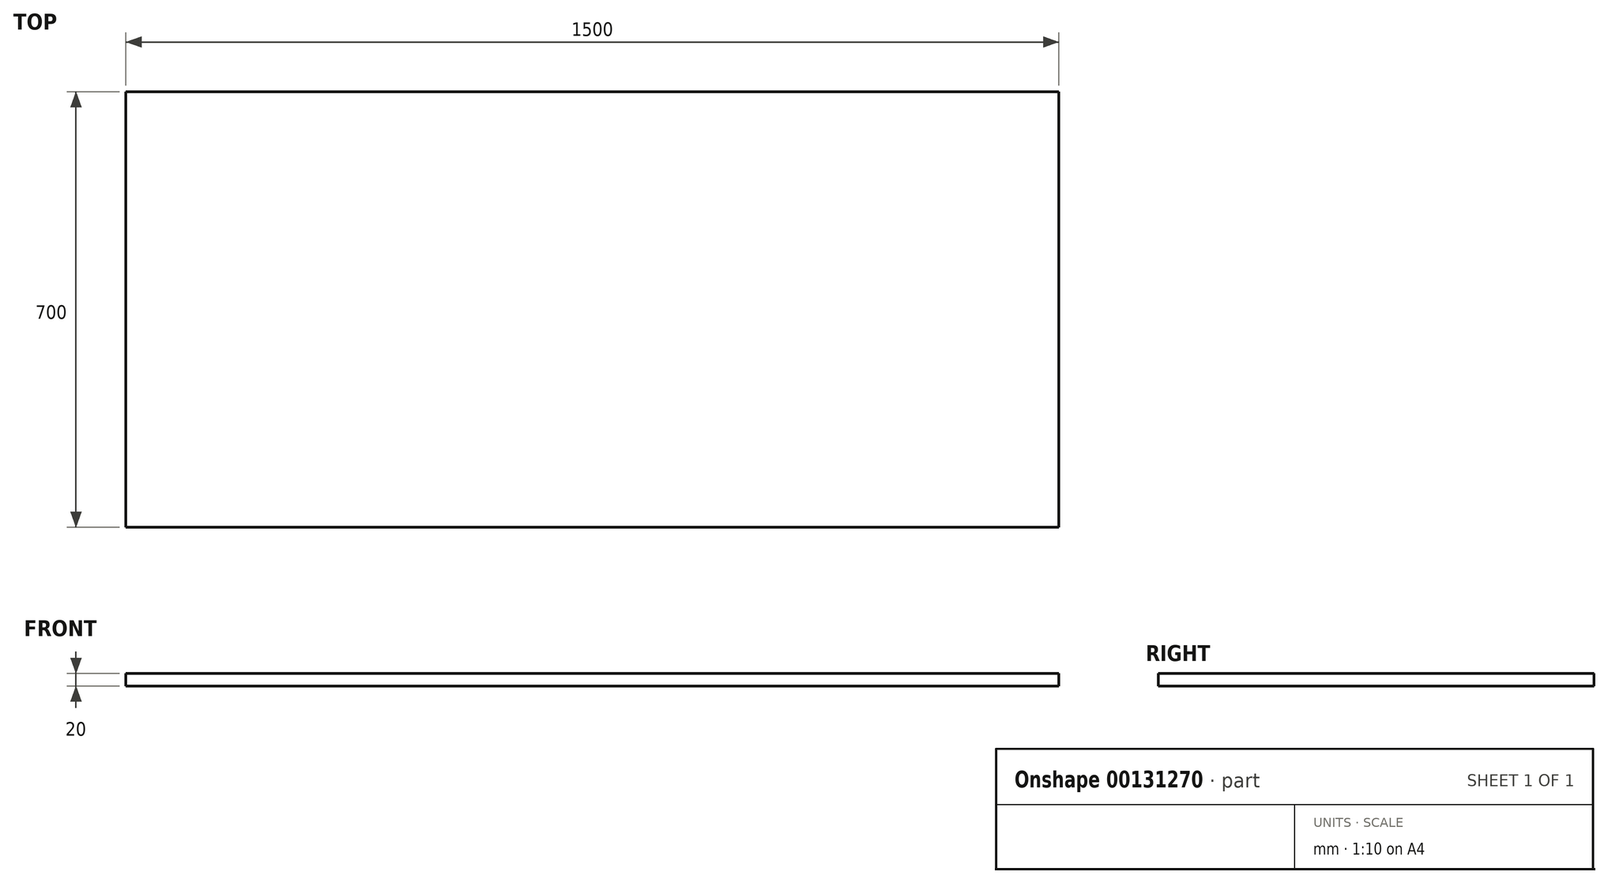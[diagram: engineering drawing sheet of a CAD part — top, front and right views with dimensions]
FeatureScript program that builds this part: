
annotation { "Feature Type Name" : "Feature", "Feature Type Description" : "" }
export const myFeature = defineFeature(function(context is Context, id is Id, definition is map)
    precondition{}
    {
        {
            var Q0;
            Q0=qCreatedBy(makeId("Top.planeOp"),FACE);
            var sketch = newSketch(context, id + "F0", { "sketchPlane" : qUnion([Q0])});
            skLineSegment(sketch, "E0.bottom", {"start": v(0, 700) * mm, "end": v(1500, 700) * mm});
            skLineSegment(sketch, "E0.top", {"start": v(0, 0) * mm, "end": v(1500, 0) * mm});
            skLineSegment(sketch, "E0.left", {"start": v(0, 700) * mm, "end": v(0, 0) * mm});
            skLineSegment(sketch, "E0.right", {"start": v(1500, 700) * mm, "end": v(1500, 0) * mm});
            skSolve(sketch);
        }
        {
            var Q0;
            Q0 = qSketchRegion(id + "F0", true);
            var Q1;
            Q1=makeQuery(id+"F0.imprint","IMPRINT",FACE,{"disambiguationData":[TD([[makeQuery(id+"F0.imprint","IMPRINT",EDGE,{"derivedFrom":sQuery(id+"F0.wireOp",EDGE,"E0.bottom")}),-1.0]])]});
            extrude(context, id + "F1", {"entities" : qUnion([Q0, Q1]), "depth" : 20 * mm});
        }
    });
